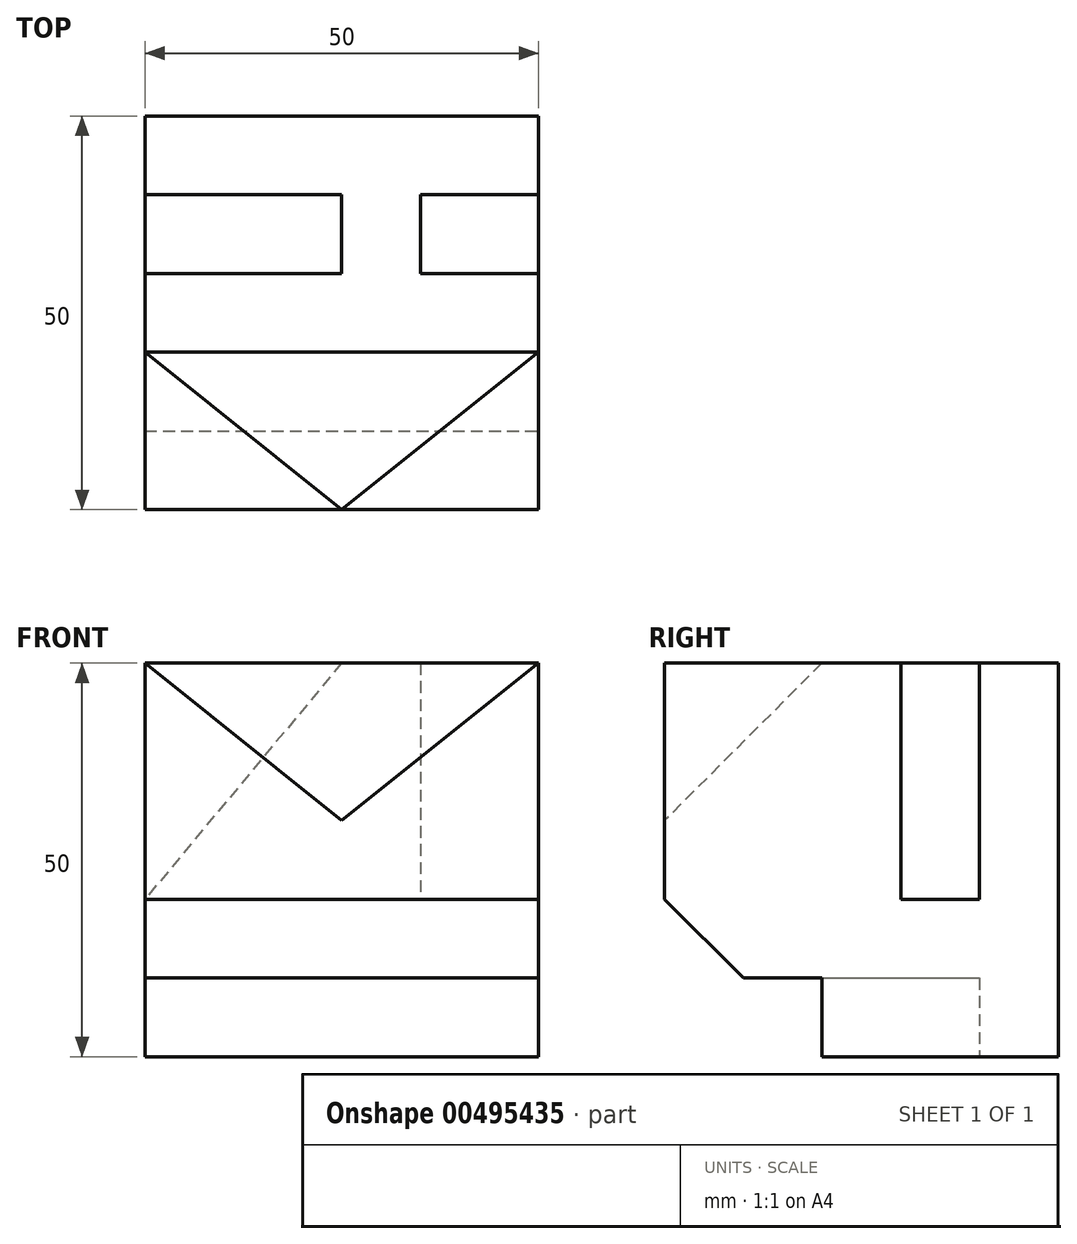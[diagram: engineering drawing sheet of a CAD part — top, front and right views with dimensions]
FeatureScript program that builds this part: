
annotation { "Feature Type Name" : "Feature", "Feature Type Description" : "" }
export const myFeature = defineFeature(function(context is Context, id is Id, definition is map)
    precondition{}
    {
        {
            var Q0;
            Q0=qCreatedBy(makeId("Top.planeOp"),FACE);
            var sketch = newSketch(context, id + "F0", { "sketchPlane" : qUnion([Q0])});
            skLineSegment(sketch, "E0.bottom", {"start": v(0, 0) * mm, "end": v(50, 0) * mm});
            skLineSegment(sketch, "E0.top", {"start": v(0, 50) * mm, "end": v(50, 50) * mm});
            skLineSegment(sketch, "E0.left", {"start": v(0, 0) * mm, "end": v(0, 50) * mm});
            skLineSegment(sketch, "E0.right", {"start": v(50, 0) * mm, "end": v(50, 50) * mm});
            skSolve(sketch);
        }
        {
            var Q0;
            Q0 = qSketchRegion(id + "F0", true);
            extrude(context, id + "F1", {"entities" : qUnion([Q0]), "depth" : 50 * mm});
        }
        {
            var Q0;
            Q0=makeQuery(id+"F1.opExtrude","CAP_FACE",FACE,{"disambiguationData":[OSD([sQuery(id+"F0.wireOp",EDGE,"E0.bottom"),sQuery(id+"F0.wireOp",EDGE,"E0.top"),sQuery(id+"F0.wireOp",EDGE,"E0.left"),sQuery(id+"F0.wireOp",EDGE,"E0.right")])],"isStart":false});
            var sketch = newSketch(context, id + "F2", { "sketchPlane" : qUnion([Q0])});
            skLineSegment(sketch, "E1", {"start": v(50, 50) * mm, "end": v(50, 40) * mm});
            skLineSegment(sketch, "E2", {"start": v(0, 50) * mm, "end": v(0, 40) * mm});
            skLineSegment(sketch, "E3", {"start": v(0, 40) * mm, "end": v(0, 30) * mm});
            skLineSegment(sketch, "E4", {"start": v(50, 40) * mm, "end": v(50, 30) * mm});
            skLineSegment(sketch, "E5", {"start": v(0, 30) * mm, "end": v(0, 20) * mm});
            skLineSegment(sketch, "E6", {"start": v(50, 30) * mm, "end": v(50, 20) * mm});
            skSolve(sketch);
        }
        {
            var Q0;
            Q0=makeQuery(id+"F1.opExtrude","SWEPT_FACE",FACE,{"disambiguationData":[OSD([sQuery(id+"F0.wireOp",EDGE,"E0.left")])]});
            var sketch = newSketch(context, id + "F3", { "sketchPlane" : qUnion([Q0])});
            skLineSegment(sketch, "E7", {"start": v(-50, 0) * mm, "end": v(-50, 20) * mm});
            skLineSegment(sketch, "E8", {"start": v(-50, 20) * mm, "end": v(-40, 20) * mm});
            skLineSegment(sketch, "E9", {"start": v(-40, 20) * mm, "end": v(-30, 20) * mm});
            skLineSegment(sketch, "E10", {"start": v(-30, 20) * mm, "end": v(-20, 20) * mm});
            skSolve(sketch);
        }
        {
            var Q0;
            Q0=makeQuery(id+"F2.imprint","IMPRINT",FACE,{"disambiguationData":[TD([[makeQuery(id+"F2.imprint","IMPRINT",EDGE,{"derivedFrom":sQuery(id+"F2.wireOp",EDGE,"E1")}),1.0]])]});
            var sketch = newSketch(context, id + "F4", { "sketchPlane" : qUnion([Q0])});
            skLineSegment(sketch, "E11", {"start": v(0, 40) * mm, "end": v(25, 40) * mm});
            skLineSegment(sketch, "E12", {"start": v(25, 40) * mm, "end": v(25, 30) * mm});
            skLineSegment(sketch, "E13", {"start": v(25, 30) * mm, "end": v(0, 30) * mm});
            skLineSegment(sketch, "E14", {"start": v(50, 40) * mm, "end": v(35, 40) * mm});
            skLineSegment(sketch, "E15", {"start": v(35, 40) * mm, "end": v(35, 30) * mm});
            skLineSegment(sketch, "E16", {"start": v(35, 30) * mm, "end": v(50, 30) * mm});
            skSolve(sketch);
        }
        {
            var Q0;
            Q0=makeQuery(id+"F1.opExtrude","CAP_EDGE",EDGE,{"disambiguationData":[OSD([sQuery(id+"F0.wireOp",EDGE,"E0.bottom")])],"isStart":false});
            cPoint(context, id + "F5", {"entities" : qUnion([Q0]), "parameter" : 0.5});
        }
        {
            var Q0;
            Q0=sQuery(id+"F4.wireOp",VERTEX,"E12.start");
            var Q1;
            Q1=sQuery(id+"F3.wireOp",VERTEX,"E9.start");
            var Q2;
            Q2 = qCreatedBy(id + "F5" ,VERTEX);
            cPlane(context, id + "F6", {"entities" : qUnion([Q0, Q1, Q2]), "cplaneType" : CPlaneType.THREE_POINT, "offset" : 25 * mm, "width" : 150 * mm, "height" : 150 * mm});
        }
        {
            var Q0;
            Q0=qCreatedBy(id+"F6.planeOp",FACE);
            var sketch = newSketch(context, id + "F7", { "sketchPlane" : qUnion([Q0])});
            skLineSegment(sketch, "E17", {"start": v(30, 15.36) * mm, "end": v(40, 15.36) * mm});
            skLineSegment(sketch, "E18", {"start": v(30, 15.36) * mm, "end": v(30, 54.42) * mm});
            skLineSegment(sketch, "E19", {"start": v(40, 54.42) * mm, "end": v(30, 54.42) * mm});
            skLineSegment(sketch, "E20", {"start": v(40, 54.42) * mm, "end": v(40, 15.36) * mm});
            skSolve(sketch);
        }
        {
            var Q0;
            Q0 = qSketchRegion(id + "F7", true);
            extrude(context, id + "F8", {"entities" : qUnion([Q0]), "operationType" : NewBodyOperationType.REMOVE, "endBound" : BoundingType.UP_TO_NEXT, "oppositeDirection" : true, "depth" : 25 * mm});
        }
        {
            var Q0;
            Q0=makeQuery(id+"F1.opExtrude","SWEPT_FACE",FACE,{"disambiguationData":[OSD([sQuery(id+"F0.wireOp",EDGE,"E0.right")])]});
            var sketch = newSketch(context, id + "F9", { "sketchPlane" : qUnion([Q0])});
            skLineSegment(sketch, "E21", {"start": v(50, 0) * mm, "end": v(50, 20) * mm});
            skLineSegment(sketch, "E22", {"start": v(50, 20) * mm, "end": v(40, 20) * mm});
            skLineSegment(sketch, "E23", {"start": v(40, 20) * mm, "end": v(30, 20) * mm});
            skSolve(sketch);
        }
        {
            var Q0;
            Q0=sQuery(id+"F9.wireOp",VERTEX,"E23.end");
            var Q1;
            Q1=sQuery(id+"F9.wireOp",VERTEX,"E23.start");
            var Q2;
            Q2=sQuery(id+"F3.wireOp",VERTEX,"E8.start");
            cPlane(context, id + "F10", {"entities" : qUnion([Q0, Q1, Q2]), "cplaneType" : CPlaneType.THREE_POINT, "offset" : 25 * mm, "width" : 150 * mm, "height" : 150 * mm});
        }
        {
            var Q0;
            Q0=qCreatedBy(id+"F10.planeOp",FACE);
            var sketch = newSketch(context, id + "F11", { "sketchPlane" : qUnion([Q0])});
            skLineSegment(sketch, "E24", {"start": v(35, -40) * mm, "end": v(35, -30) * mm});
            skLineSegment(sketch, "E25", {"start": v(35, -30) * mm, "end": v(50, -30) * mm});
            skLineSegment(sketch, "E26", {"start": v(50, -30) * mm, "end": v(50, -40) * mm});
            skLineSegment(sketch, "E27", {"start": v(50, -40) * mm, "end": v(35, -40) * mm});
            skSolve(sketch);
        }
        {
            var Q0;
            Q0 = qSketchRegion(id + "F11", true);
            extrude(context, id + "F12", {"entities" : qUnion([Q0]), "operationType" : NewBodyOperationType.REMOVE, "endBound" : BoundingType.UP_TO_NEXT, "oppositeDirection" : true, "depth" : 25 * mm});
        }
        {
            var Q0;
            Q0=makeQuery(id+"F1.opExtrude","SWEPT_FACE",FACE,{"disambiguationData":[OSD([sQuery(id+"F0.wireOp",EDGE,"E0.bottom")])]});
            var sketch = newSketch(context, id + "F13", { "sketchPlane" : qUnion([Q0])});
            skLineSegment(sketch, "E28", {"start": v(0, 50) * mm, "end": v(25, 30) * mm});
            skLineSegment(sketch, "E29", {"start": v(25, 30) * mm, "end": v(50, 50) * mm});
            skLineSegment(sketch, "E30", {"start": v(50, 50) * mm, "end": v(0, 50) * mm});
            skSolve(sketch);
        }
        {
            var Q0;
            Q0=makeQuery(id+"F4.imprint","IMPRINT",FACE,{"disambiguationData":[TD([[makeQuery(id+"F4.imprint","IMPRINT",EDGE,{"derivedFrom":sQuery(id+"F4.wireOp",EDGE,"E11")}),1.0]])]});
            var sketch = newSketch(context, id + "F14", { "sketchPlane" : qUnion([Q0])});
            skLineSegment(sketch, "E31.bottom", {"start": v(0, 0) * mm, "end": v(50, 0) * mm});
            skLineSegment(sketch, "E31.top", {"start": v(0, 20) * mm, "end": v(50, 20) * mm});
            skLineSegment(sketch, "E31.left", {"start": v(0, 0) * mm, "end": v(0, 20) * mm});
            skLineSegment(sketch, "E31.right", {"start": v(50, 0) * mm, "end": v(50, 20) * mm});
            skSolve(sketch);
        }
        {
            var Q0;
            Q0=sQuery(id+"F14.wireOp",EDGE,"E31.top");
            cPoint(context, id + "F15", {"entities" : qUnion([Q0]), "parameter" : 0.5});
        }
        {
            var Q0;
            Q0 = qCreatedBy(id + "F15" ,VERTEX);
            var Q1;
            Q1=sQuery(id+"F14.wireOp",VERTEX,"E31.right.start");
            var Q2;
            Q2=sQuery(id+"F13.wireOp",VERTEX,"E29.start");
            cPlane(context, id + "F16", {"entities" : qUnion([Q0, Q1, Q2]), "cplaneType" : CPlaneType.THREE_POINT, "offset" : 25 * mm, "width" : 150 * mm, "height" : 150 * mm});
        }
        {
            var Q0;
            Q0=sQuery(id+"F2.wireOp",VERTEX,"E5.end");
            var Q1;
            Q1=sQuery(id+"F2.wireOp",VERTEX,"E6.end");
            var Q2;
            Q2=sQuery(id+"F13.wireOp",VERTEX,"E29.start");
            cPlane(context, id + "F17", {"entities" : qUnion([Q0, Q1, Q2]), "cplaneType" : CPlaneType.THREE_POINT, "offset" : 25 * mm, "width" : 150 * mm, "height" : 150 * mm});
        }
        {
            var Q0;
            Q0=makeQuery(id+"F13.imprint","IMPRINT",FACE,{"disambiguationData":[TD([[makeQuery(id+"F13.imprint","IMPRINT",EDGE,{"derivedFrom":sQuery(id+"F13.wireOp",EDGE,"E28")}),1.0]])]});
            var Q1;
            Q1=qCreatedBy(id+"F17.planeOp",FACE);
            extrude(context, id + "F18", {"entities" : qUnion([Q0]), "operationType" : NewBodyOperationType.REMOVE, "endBound" : BoundingType.UP_TO_SURFACE, "oppositeDirection" : true, "depth" : 25 * mm, "endBoundEntityFace" : qUnion([Q1]), "offsetDistance" : 25 * mm});
        }
        {
            var Q0;
            {var subQ3=sQuery(id+"F9.wireOp",EDGE,"E21");Q0=makeQuery(id+"F9.imprint","IMPRINT",FACE,{"disambiguationData":[TD([[makeQuery(id+"F9.imprint","IMPRINT",EDGE,{"derivedFrom":subQ3}),-1.0]])]});}
            var sketch = newSketch(context, id + "F19", { "sketchPlane" : qUnion([Q0])});
            skLineSegment(sketch, "E32", {"start": v(0, 0) * mm, "end": v(0, 10) * mm});
            skSolve(sketch);
        }
        {
            var Q0;
            Q0=makeQuery(id+"F1.opExtrude","CAP_FACE",FACE,{"disambiguationData":[OSD([sQuery(id+"F0.wireOp",EDGE,"E0.bottom"),sQuery(id+"F0.wireOp",EDGE,"E0.top"),sQuery(id+"F0.wireOp",EDGE,"E0.left"),sQuery(id+"F0.wireOp",EDGE,"E0.right")])],"isStart":true});
            var sketch = newSketch(context, id + "F20", { "sketchPlane" : qUnion([Q0])});
            skLineSegment(sketch, "E33", {"start": v(50, 0) * mm, "end": v(50, -20) * mm});
            skLineSegment(sketch, "E34.bottom", {"start": v(50, 0) * mm, "end": v(0, 0) * mm});
            skLineSegment(sketch, "E34.top", {"start": v(50, -20) * mm, "end": v(0, -20) * mm});
            skLineSegment(sketch, "E34.right", {"start": v(0, 0) * mm, "end": v(0, -20) * mm});
            skSolve(sketch);
        }
        {
            var Q0;
            Q0 = qSketchRegion(id + "F20", true);
            extrude(context, id + "F21", {"entities" : qUnion([Q0]), "operationType" : NewBodyOperationType.REMOVE, "oppositeDirection" : true, "depth" : 10 * mm, "offsetDistance" : 25 * mm});
        }
        {
            var Q0;
            {var subQ3=sQuery(id+"F9.wireOp",EDGE,"E21");Q0=makeQuery(id+"F9.imprint","IMPRINT",FACE,{"disambiguationData":[TD([[makeQuery(id+"F9.imprint","IMPRINT",EDGE,{"derivedFrom":subQ3}),-1.0]])]});}
            var sketch = newSketch(context, id + "F22", { "sketchPlane" : qUnion([Q0])});
            skLineSegment(sketch, "E35", {"start": v(0, 10) * mm, "end": v(0, 20) * mm});
            skLineSegment(sketch, "E36", {"start": v(0, 10) * mm, "end": v(10, 10) * mm});
            skLineSegment(sketch, "E37", {"start": v(0, 20) * mm, "end": v(10, 10) * mm});
            skSolve(sketch);
        }
        {
            var Q0;
            Q0 = qSketchRegion(id + "F22", true);
            extrude(context, id + "F23", {"entities" : qUnion([Q0]), "operationType" : NewBodyOperationType.REMOVE, "endBound" : BoundingType.UP_TO_NEXT, "oppositeDirection" : true, "depth" : 25 * mm, "offsetDistance" : 25 * mm});
        }
        {
            var Q0;
            Q0=makeQuery(id+"F1.opExtrude","CAP_FACE",FACE,{"disambiguationData":[OSD([sQuery(id+"F0.wireOp",EDGE,"E0.bottom"),sQuery(id+"F0.wireOp",EDGE,"E0.top"),sQuery(id+"F0.wireOp",EDGE,"E0.left"),sQuery(id+"F0.wireOp",EDGE,"E0.right")])],"isStart":true});
            var sketch = newSketch(context, id + "F24", { "sketchPlane" : qUnion([Q0])});
            skLineSegment(sketch, "E38", {"start": v(0, -50) * mm, "end": v(0, -40) * mm});
            skLineSegment(sketch, "E39", {"start": v(50, -20) * mm, "end": v(0, -40) * mm});
            skLineSegment(sketch, "E40", {"start": v(50, -20) * mm, "end": v(0, -20) * mm});
            skLineSegment(sketch, "E41", {"start": v(0, -20) * mm, "end": v(0, -40) * mm});
            skSolve(sketch);
        }
        {
            var Q0;
            Q0 = qSketchRegion(id + "F24", true);
            extrude(context, id + "F25", {"entities" : qUnion([Q0]), "operationType" : NewBodyOperationType.REMOVE, "oppositeDirection" : true, "depth" : 10 * mm, "offsetDistance" : 25 * mm});
        }
    });
